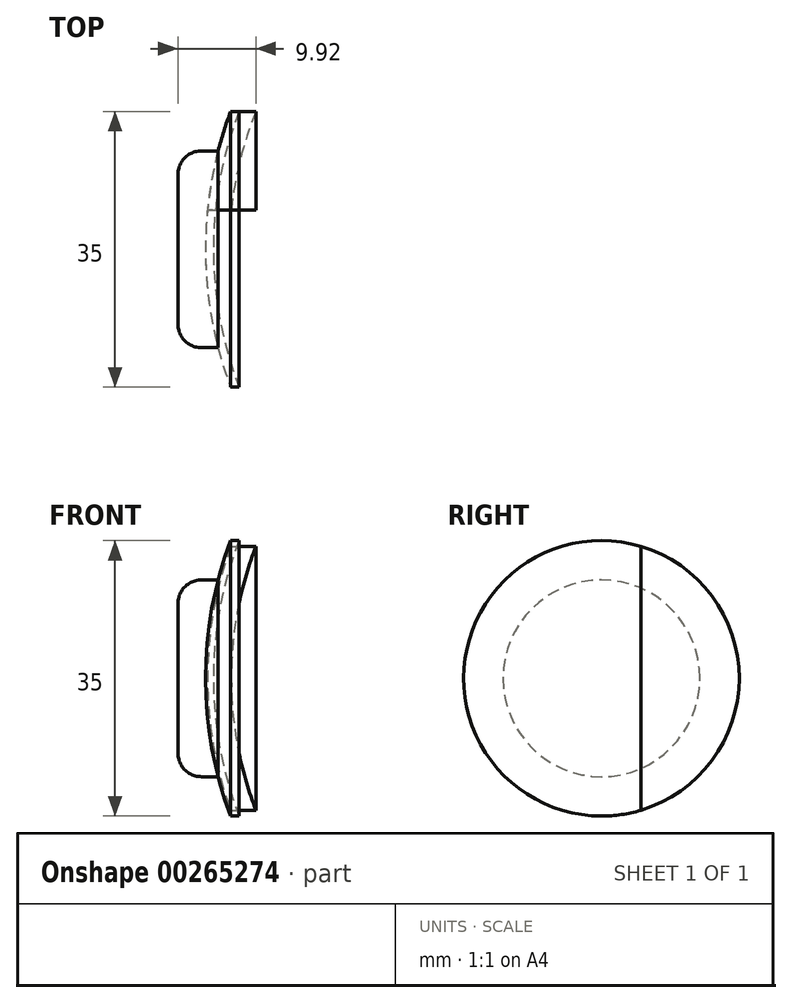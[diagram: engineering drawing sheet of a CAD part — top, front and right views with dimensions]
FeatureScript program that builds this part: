
annotation { "Feature Type Name" : "Feature", "Feature Type Description" : "" }
export const myFeature = defineFeature(function(context is Context, id is Id, definition is map)
    precondition{}
    {
        {
            var Q0;
            Q0=qCreatedBy(makeId("Front.planeOp"),FACE);
            var sketch = newSketch(context, id + "F0", { "sketchPlane" : qUnion([Q0])});
            skArc(sketch, "E0", {"start": v(0, -50) * mm, "mid": v(50, 0) * mm, "end": v(0, 50) * mm});
            skLineSegment(sketch, "E1", {"start": v(0, 50) * mm, "end": v(0, -50) * mm});
            skSolve(sketch);
        }
        {
            var Q0;
            Q0=makeQuery(id+"F0.imprint","IMPRINT",FACE,{"disambiguationData":[TD([[makeQuery(id+"F0.imprint","IMPRINT",EDGE,{"derivedFrom":sQuery(id+"F0.wireOp",EDGE,"E0")}),1.0]])]});
            var Q1;
            Q1=sQuery(id+"F0.wireOp",EDGE,"E1");
            revolve(context, id + "F1", {"entities" : qUnion([Q0]), "axis" : qUnion([Q1]), "revolveType" : RevolveType.FULL});
        }
        {
            var Q0;
            Q0=qCreatedBy(makeId("Top.planeOp"),FACE);
            var sketch = newSketch(context, id + "F2", { "sketchPlane" : qUnion([Q0])});
            skArc(sketch, "E2", {"start": v(49.75, -5) * mm, "mid": v(50, 0) * mm, "end": v(49.75, 5) * mm});
            skLineSegment(sketch, "E3", {"start": v(49.75, -5) * mm, "end": v(-49.75, -5) * mm});
            skLineSegment(sketch, "E4.MirrorCS", {"start": v(49.75, 5) * mm, "end": v(-49.75, 5) * mm});
            skArc(sketch, "E5.trimOffspring", {"start": v(-49.75, 5) * mm, "mid": v(-50, 0) * mm, "end": v(-49.75, -5) * mm});
            skSolve(sketch);
        }
        {
            var Q0;
            Q0=makeQuery(id+"F2.imprint","IMPRINT",FACE,{"disambiguationData":[TD([[makeQuery(id+"F2.imprint","IMPRINT",EDGE,{"derivedFrom":sQuery(id+"F2.wireOp",EDGE,"E2")}),1.0]])]});
            extrude(context, id + "F3", {"entities" : qUnion([Q0]), "operationType" : NewBodyOperationType.REMOVE, "endBound" : BoundingType.THROUGH_ALL, "oppositeDirection" : true, "depth" : 25 * mm, "hasSecondDirection" : true, "secondDirectionBound" : SecondDirectionBoundingType.THROUGH_ALL, "secondDirectionOppositeDirection" : false, "secondDirectionDepth" : 25 * mm});
        }
        {
            var Q0;
            Q0=makeQuery(id+"F3.boolean.opBoolean","COPY",FACE,{"derivedFrom":makeQuery(id+"F3.opExtrude","SWEPT_FACE",FACE,{"disambiguationData":[OSD([sQuery(id+"F2.wireOp",EDGE,"E4.MirrorCS")])]})});
            shell(context, id + "F4", {"entities" : qUnion([Q0]), "thickness" : 3 * mm});
        }
        {
            var Q0;
            Q0=makeQuery(id+"F3.boolean.opBoolean","COPY",FACE,{"derivedFrom":makeQuery(id+"F3.opExtrude","SWEPT_FACE",FACE,{"disambiguationData":[OSD([sQuery(id+"F2.wireOp",EDGE,"E3")])]})});
            shell(context, id + "F5", {"entities" : qUnion([Q0]), "thickness" : 3 * mm});
        }
        {
            var Q0;
            Q0=qCreatedBy(makeId("Right.planeOp"),FACE);
            var sketch = newSketch(context, id + "F6", { "sketchPlane" : qUnion([Q0])});
            skCircle(sketch, "E6", {"center": v(0, 0) * mm, "radius": 17.5 * mm});
            skSolve(sketch);
        }
        {
            var Q0;
            Q0=makeQuery(id+"F6.imprint","IMPRINT",FACE,{"disambiguationData":[TD([[makeQuery(id+"F6.imprint","IMPRINT",EDGE,{"derivedFrom":sQuery(id+"F6.wireOp",EDGE,"E6")}),1.0]])]});
            extrude(context, id + "F7", {"entities" : qUnion([Q0]), "operationType" : NewBodyOperationType.REMOVE, "endBound" : BoundingType.THROUGH_ALL, "oppositeDirection" : true, "depth" : 25 * mm});
        }
        {
            var Q0;
            Q0=qCreatedBy(makeId("Right.planeOp"),FACE);
            var sketch = newSketch(context, id + "F8", { "sketchPlane" : qUnion([Q0])});
            skCircle(sketch, "E7", {"center": v(0, 0) * mm, "radius": 49.5 * mm});
            skCircle(sketch, "E8.0", {"center": v(0, 0) * mm, "radius": 46.5 * mm});
            skLineSegment(sketch, "E9.0", {"start": v(-5, 49.75) * mm, "end": v(-5, -49.75) * mm});
            skLineSegment(sketch, "E10.0", {"start": v(5, 49.75) * mm, "end": v(5, -49.75) * mm});
            skLineSegment(sketch, "E11", {"start": v(55.36, 0) * mm, "end": v(-64.9, 0) * mm});
            skPoint(sketch, "E11.endSnap0", {"position": v(-5, 0) * mm});
            skSolve(sketch);
        }
        {
            var Q0;
            {var subQ0=sQuery(id+"F8.wireOp",EDGE,"E10.0");var subQ1=sQuery(id+"F8.wireOp",EDGE,"E7");var subQ2=makeQuery(id+"F8.imprint","INTERSECT",VERTEX,{"disambiguationData":[OD(0.0)],"derivedFrom":[subQ1,subQ0]});Q0=makeQuery(id+"F8.imprint","IMPRINT",FACE,{"disambiguationData":[TD([[makeQuery(id+"F8.imprint","IMPRINT",EDGE,{"disambiguationData":[TD([[subQ2,-1.0]])],"derivedFrom":subQ1}),1.0]])]});}
            var Q1;
            Q1=sQuery(id+"F8.wireOp",EDGE,"E11");
            revolve(context, id + "F9", {"entities" : qUnion([Q0]), "axis" : qUnion([Q1]), "revolveType" : RevolveType.FULL});
        }
        {
            var Q0;
            Q0=qCreatedBy(makeId("Top.planeOp"),FACE);
            var sketch = newSketch(context, id + "F10", { "sketchPlane" : qUnion([Q0])});
            skArc(sketch, "E12", {"start": v(0, 49.5) * mm, "mid": v(-49.5, 0) * mm, "end": v(0, -49.5) * mm});
            skArc(sketch, "E13", {"start": v(0, 48.5) * mm, "mid": v(-48.5, 0) * mm, "end": v(0, -48.5) * mm});
            skLineSegment(sketch, "E14", {"start": v(0, 49.5) * mm, "end": v(0, -49.5) * mm});
            skSolve(sketch);
        }
        {
            var Q0;
            {var subQ0=sQuery(id+"F10.wireOp",EDGE,"E12");Q0=makeQuery(id+"F10.imprint","IMPRINT",FACE,{"disambiguationData":[TD([[makeQuery(id+"F10.imprint","IMPRINT",EDGE,{"derivedFrom":subQ0}),1.0]])]});}
            var Q1;
            Q1=sQuery(id+"F10.wireOp",EDGE,"E14");
            revolve(context, id + "F11", {"entities" : qUnion([Q0]), "axis" : qUnion([Q1]), "revolveType" : RevolveType.FULL});
        }
        {
            var Q0;
            Q0=qCreatedBy(makeId("Right.planeOp"),FACE);
            var sketch = newSketch(context, id + "F12", { "sketchPlane" : qUnion([Q0])});
            skCircle(sketch, "E15", {"center": v(0, 0) * mm, "radius": 17.5 * mm});
            skSolve(sketch);
        }
        {
            var Q0;
            Q0=makeQuery(id+"F12.imprint","IMPRINT",FACE,{"disambiguationData":[TD([[makeQuery(id+"F12.imprint","IMPRINT",EDGE,{"derivedFrom":sQuery(id+"F12.wireOp",EDGE,"E15")}),1.0]])]});
            var Q1;
            Q1=makeQuery(id+"F11.opRevolve","SWEPT_BODY",BODY,{"disambiguationData":[OSD([sQuery(id+"F10.wireOp",EDGE,"E12"),sQuery(id+"F10.wireOp",EDGE,"E13"),sQuery(id+"F10.wireOp",EDGE,"E14")])]});
            extrude(context, id + "F13", {"entities" : qUnion([Q0]), "operationType" : NewBodyOperationType.INTERSECT, "endBound" : BoundingType.THROUGH_ALL, "oppositeDirection" : true, "endBoundEntityBody" : qUnion([Q1]), "depth" : 25 * mm});
        }
        {
            var Q0;
            Q0=qCreatedBy(makeId("Right.planeOp"),FACE);
            cPlane(context, id + "F14", {"entities" : qUnion([Q0]), "cplaneType" : CPlaneType.OFFSET, "offset" : 53 * mm, "oppositeDirection" : true, "width" : 150 * mm, "height" : 150 * mm});
        }
        {
            var Q0;
            Q0=qCreatedBy(id+"F14.planeOp",FACE);
            var sketch = newSketch(context, id + "F15", { "sketchPlane" : qUnion([Q0])});
            skCircle(sketch, "E16", {"center": v(0, 0) * mm, "radius": 12.5 * mm});
            skSolve(sketch);
        }
        {
            var Q0;
            Q0=makeQuery(id+"F15.imprint","IMPRINT",FACE,{"disambiguationData":[TD([[makeQuery(id+"F15.imprint","IMPRINT",EDGE,{"derivedFrom":sQuery(id+"F15.wireOp",EDGE,"E16")}),1.0]])]});
            extrude(context, id + "F16", {"entities" : qUnion([Q0]), "endBound" : BoundingType.UP_TO_NEXT, "depth" : 25 * mm});
        }
        {
            var Q0;
            Q0=makeQuery(id+"F16.opExtrude","CAP_EDGE",EDGE,{"disambiguationData":[OSD([sQuery(id+"F15.wireOp",EDGE,"E16")])],"isStart":true});
            fillet(context, id + "F17", {"entities" : qUnion([Q0]), "radius" : 3 * mm, "tangentPropagation" : true, "allowEdgeOverflow" : false});
        }
    });
